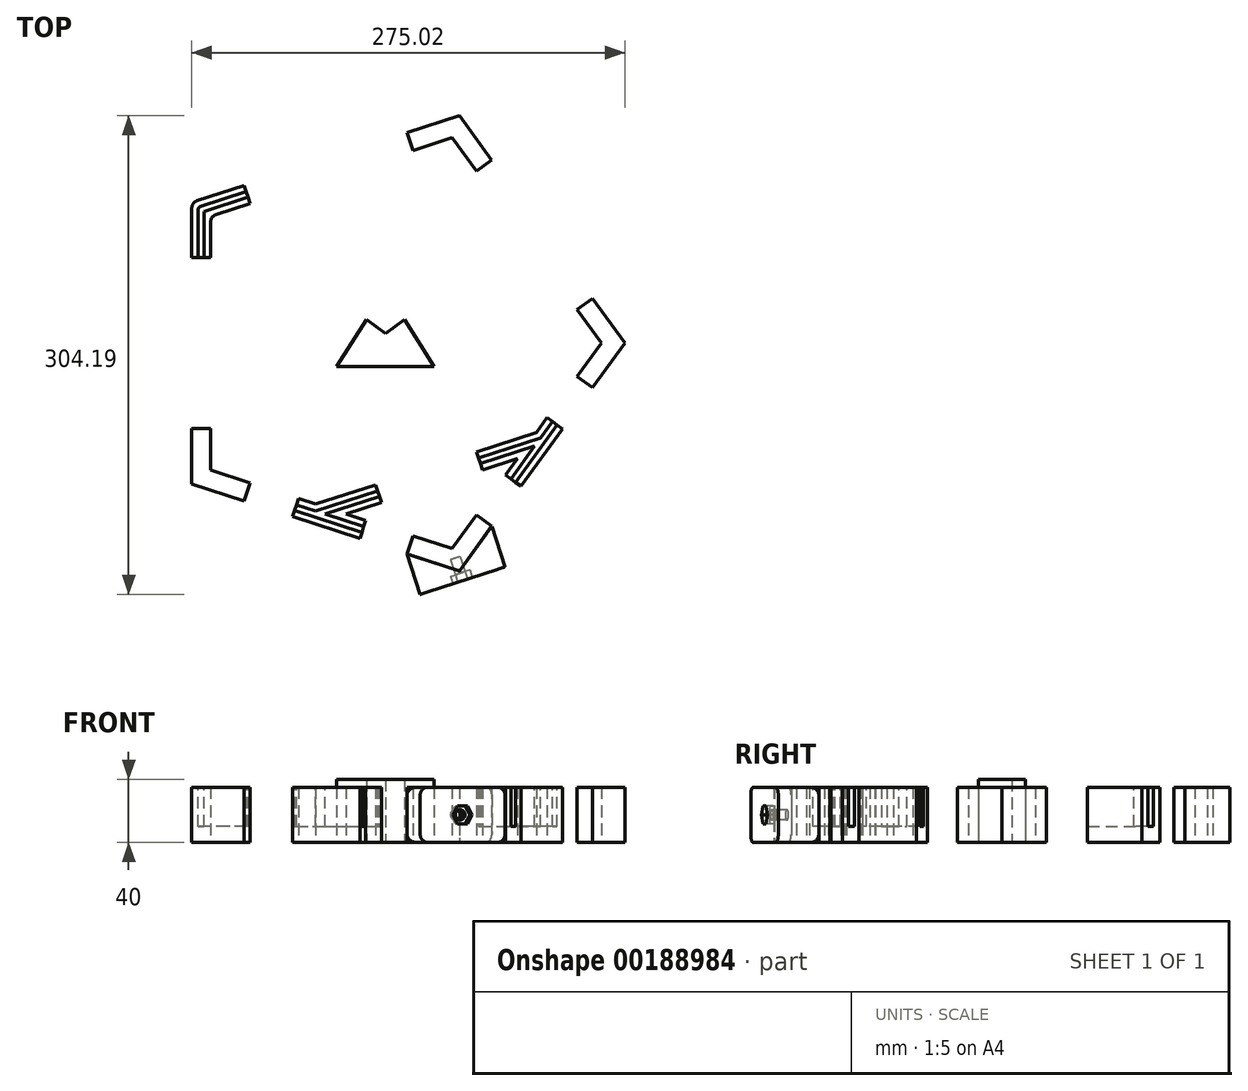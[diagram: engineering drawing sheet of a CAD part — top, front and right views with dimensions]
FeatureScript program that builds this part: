
annotation { "Feature Type Name" : "Feature", "Feature Type Description" : "" }
export const myFeature = defineFeature(function(context is Context, id is Id, definition is map)
    precondition{}
    {
        {
            var Q0;
            Q0=qCreatedBy(makeId("Top.planeOp"),FACE);
            var sketch = newSketch(context, id + "F0", { "sketchPlane" : qUnion([Q0])});
            skCircle(sketch, "E0.cCircle", {"center": v(0, 0) * mm, "radius": 117 * mm, "construction": true});
            skLineSegment(sketch, "E0.0", {"start": v(-117, 85) * mm, "end": v(44.69, 137.53) * mm, "construction": true});
            skLineSegment(sketch, "E0.1", {"start": v(44.69, 137.53) * mm, "end": v(144.61, 0) * mm, "construction": true});
            skLineSegment(sketch, "E0.2", {"start": v(144.61, 0) * mm, "end": v(44.69, -137.53) * mm, "construction": true});
            skLineSegment(sketch, "E0.3", {"start": v(44.69, -137.53) * mm, "end": v(-117, -85) * mm, "construction": true});
            skLineSegment(sketch, "E0.4", {"start": v(-117, -85) * mm, "end": v(-117, 85) * mm, "construction": true});
            skPoint(sketch, "E0.0.midPoint", {"position": v(-36.15, 111.27) * mm});
            skLineSegment(sketch, "E1", {"start": v(-123, 89.36) * mm, "end": v(-89.7, 100.17) * mm});
            skLineSegment(sketch, "E2", {"start": v(-123, 54.36) * mm, "end": v(-123, 89.36) * mm});
            skLineSegment(sketch, "E3.MirrorCS", {"start": v(-111, 54.36) * mm, "end": v(-111, 80.64) * mm});
            skLineSegment(sketch, "E4.MirrorCS", {"start": v(-111, 80.64) * mm, "end": v(-86, 88.76) * mm});
            skPoint(sketch, "E5.orphan", {"position": v(-127.63, 87.85) * mm});
            skPoint(sketch, "E6.orphan", {"position": v(-123, 104.04) * mm});
            skPoint(sketch, "E7.orphan", {"position": v(-111, 104.04) * mm});
            skPoint(sketch, "E8.orphan", {"position": v(-123.92, 76.44) * mm});
            skLineSegment(sketch, "E9", {"start": v(-123, 54.36) * mm, "end": v(-111, 54.36) * mm});
            skLineSegment(sketch, "E10", {"start": v(-86, 88.76) * mm, "end": v(-89.7, 100.17) * mm});
            skPoint(sketch, "E11.MirrorP", {"position": v(-127.63, -87.85) * mm});
            skPoint(sketch, "E12.MirrorP", {"position": v(-123, -104.04) * mm});
            skPoint(sketch, "E13.MirrorP", {"position": v(-111, -104.04) * mm});
            skPoint(sketch, "E14.MirrorP", {"position": v(-123.92, -76.44) * mm});
            skLineSegment(sketch, "E15.MirrorCS", {"start": v(-86, -88.76) * mm, "end": v(-89.7, -100.17) * mm});
            skLineSegment(sketch, "E16.MirrorCS", {"start": v(-123, -54.36) * mm, "end": v(-111, -54.36) * mm});
            skLineSegment(sketch, "E17.MirrorCS", {"start": v(-111, -80.64) * mm, "end": v(-86, -88.76) * mm});
            skLineSegment(sketch, "E18.MirrorCS", {"start": v(-111, -54.36) * mm, "end": v(-111, -80.64) * mm});
            skLineSegment(sketch, "E19.MirrorCS", {"start": v(-123, -54.36) * mm, "end": v(-123, -89.36) * mm});
            skLineSegment(sketch, "E20.MirrorCS", {"start": v(-123, -89.36) * mm, "end": v(-89.7, -100.17) * mm});
            skLineSegment(sketch, "E21.MirrorCS", {"start": v(-117, 85) * mm, "end": v(-117, -85) * mm, "construction": true});
            skLineSegment(sketch, "E22.MirrorCS", {"start": v(-117, -85) * mm, "end": v(44.69, -137.53) * mm, "construction": true});
            skLineSegment(sketch, "E23", {"start": v(-36.15, -111.27) * mm, "end": v(-46.52, -143.17) * mm, "construction": true});
            skLineSegment(sketch, "E24.MirrorCS", {"start": v(44.69, -137.53) * mm, "end": v(144.61, 0) * mm, "construction": true});
            skPoint(sketch, "E25.MirrorP", {"position": v(51.62, -146.1) * mm});
            skLineSegment(sketch, "E26.MirrorCS", {"start": v(67.55, -116.27) * mm, "end": v(46.98, -144.59) * mm});
            skPoint(sketch, "E27.MirrorP", {"position": v(160.66, 11.88) * mm});
            skLineSegment(sketch, "E28.MirrorCS", {"start": v(17.4, -122.36) * mm, "end": v(13.7, -133.77) * mm});
            skLineSegment(sketch, "E29.MirrorCS", {"start": v(121.75, 21.26) * mm, "end": v(131.45, 28.32) * mm});
            skLineSegment(sketch, "E30.MirrorCS", {"start": v(131.45, -28.32) * mm, "end": v(121.75, -21.26) * mm});
            skLineSegment(sketch, "E31.MirrorCS", {"start": v(137.2, 0) * mm, "end": v(121.75, 21.26) * mm});
            skLineSegment(sketch, "E32.MirrorCS", {"start": v(121.75, -21.26) * mm, "end": v(137.2, 0) * mm});
            skLineSegment(sketch, "E33.MirrorCS", {"start": v(131.45, -28.32) * mm, "end": v(152.03, 0) * mm});
            skLineSegment(sketch, "E34.MirrorCS", {"start": v(152.03, 0) * mm, "end": v(131.45, 28.32) * mm});
            skPoint(sketch, "E35.MirrorP", {"position": v(28.64, -149.41) * mm});
            skPoint(sketch, "E36.MirrorP", {"position": v(55.33, -134.68) * mm});
            skPoint(sketch, "E37.MirrorP", {"position": v(150.95, 18.93) * mm});
            skPoint(sketch, "E38.MirrorP", {"position": v(154.9, -3.95) * mm});
            skLineSegment(sketch, "E39.MirrorCS", {"start": v(67.55, -116.27) * mm, "end": v(57.84, -109.22) * mm});
            skLineSegment(sketch, "E40.MirrorCS", {"start": v(46.98, -144.59) * mm, "end": v(13.7, -133.77) * mm});
            skLineSegment(sketch, "E41.MirrorCS", {"start": v(42.4, -130.48) * mm, "end": v(17.4, -122.36) * mm});
            skLineSegment(sketch, "E42.MirrorCS", {"start": v(57.84, -109.22) * mm, "end": v(42.4, -130.48) * mm});
            skPoint(sketch, "E43.MirrorP", {"position": v(38.35, -156.47) * mm});
            skPoint(sketch, "E44.MirrorP", {"position": v(145.19, -11) * mm});
            skLineSegment(sketch, "E45", {"start": v(94.65, 68.77) * mm, "end": v(113.34, 82.34) * mm, "construction": true});
            skLineSegment(sketch, "E46.MirrorCS", {"start": v(44.69, 137.53) * mm, "end": v(-117, 85) * mm, "construction": true});
            skLineSegment(sketch, "E47.MirrorCS", {"start": v(46.98, 144.59) * mm, "end": v(67.55, 116.27) * mm});
            skPoint(sketch, "E48.MirrorP", {"position": v(60.94, 149.12) * mm});
            skPoint(sketch, "E49.MirrorP", {"position": v(44.11, 148.53) * mm});
            skPoint(sketch, "E50.MirrorP", {"position": v(34.4, 141.48) * mm});
            skLineSegment(sketch, "E51.MirrorCS", {"start": v(13.7, 133.77) * mm, "end": v(46.98, 144.59) * mm});
            skLineSegment(sketch, "E52.MirrorCS", {"start": v(42.4, 130.48) * mm, "end": v(57.84, 109.22) * mm});
            skPoint(sketch, "E53.MirrorP", {"position": v(64.65, 137.71) * mm});
            skLineSegment(sketch, "E54.MirrorCS", {"start": v(144.61, 0) * mm, "end": v(44.69, 137.53) * mm, "construction": true});
            skLineSegment(sketch, "E55.MirrorCS", {"start": v(57.84, 109.22) * mm, "end": v(67.55, 116.27) * mm});
            skLineSegment(sketch, "E56.MirrorCS", {"start": v(17.4, 122.36) * mm, "end": v(42.4, 130.48) * mm});
            skLineSegment(sketch, "E57.MirrorCS", {"start": v(13.7, 133.77) * mm, "end": v(17.4, 122.36) * mm});
            skLineSegment(sketch, "E58", {"start": v(-81.04, -120.55) * mm, "end": v(144.28, -47.34) * mm, "construction": true});
            skLineSegment(sketch, "E59", {"start": v(44.69, -137.53) * mm, "end": v(54.4, -134.38) * mm});
            skLineSegment(sketch, "E60", {"start": v(-16.2, -124.06) * mm, "end": v(-59, -110.15) * mm});
            skLineSegment(sketch, "E61.MirrorCS", {"start": v(-12.49, -112.65) * mm, "end": v(-24.89, -108.62) * mm});
            skLineSegment(sketch, "E62", {"start": v(-44.3, -102.3) * mm, "end": v(-6.26, -89.95) * mm});
            skLineSegment(sketch, "E63.MirrorCS", {"start": v(-34.6, -111.77) * mm, "end": v(-34.58, -111.77) * mm});
            skLineSegment(sketch, "E64", {"start": v(-55.29, -98.74) * mm, "end": v(-59, -110.15) * mm});
            skLineSegment(sketch, "E65", {"start": v(-12.49, -112.65) * mm, "end": v(-16.2, -124.06) * mm});
            skPoint(sketch, "E66.orphan", {"position": v(-40.6, -113.72) * mm});
            skLineSegment(sketch, "E67.trimOffspring", {"start": v(-24.89, -108.62) * mm, "end": v(-2.55, -101.36) * mm});
            skLineSegment(sketch, "E68.trimOffspring", {"start": v(-44.3, -102.3) * mm, "end": v(-55.29, -98.74) * mm});
            skLineSegment(sketch, "E69", {"start": v(-6.26, -89.95) * mm, "end": v(-2.55, -101.36) * mm});
            skLineSegment(sketch, "E70", {"start": v(-36.15, 111.27) * mm, "end": v(42.4, -130.48) * mm, "construction": true});
            skLineSegment(sketch, "E71.MirrorCS", {"start": v(93.69, -70.1) * mm, "end": v(93.67, -70.1) * mm});
            skLineSegment(sketch, "E72.MirrorCS", {"start": v(102.77, -47.39) * mm, "end": v(112.47, -54.44) * mm});
            skLineSegment(sketch, "E73.MirrorCS", {"start": v(95.98, -56.73) * mm, "end": v(102.77, -47.39) * mm});
            skLineSegment(sketch, "E74.MirrorCS", {"start": v(76.32, -83.8) * mm, "end": v(86.02, -90.85) * mm});
            skLineSegment(sketch, "E75.MirrorCS", {"start": v(95.98, -56.73) * mm, "end": v(57.94, -69.09) * mm});
            skPoint(sketch, "E76.MirrorP", {"position": v(99.69, -68.14) * mm});
            skLineSegment(sketch, "E77.MirrorCS", {"start": v(83.98, -73.24) * mm, "end": v(61.64, -80.5) * mm});
            skLineSegment(sketch, "E78.MirrorCS", {"start": v(86.02, -90.85) * mm, "end": v(112.47, -54.44) * mm});
            skLineSegment(sketch, "E79.MirrorCS", {"start": v(57.94, -69.09) * mm, "end": v(61.64, -80.5) * mm});
            skLineSegment(sketch, "E80.MirrorCS", {"start": v(76.32, -83.8) * mm, "end": v(83.98, -73.24) * mm});
            skLineSegment(sketch, "E81", {"start": v(22.07, -159.6) * mm, "end": v(75.94, -142.1) * mm});
            skLineSegment(sketch, "E82", {"start": v(67.59, -116.39) * mm, "end": v(75.94, -142.1) * mm});
            skLineSegment(sketch, "E83.MirrorCS", {"start": v(13.73, -133.89) * mm, "end": v(22.08, -159.6) * mm});
            skLineSegment(sketch, "E84", {"start": v(13.73, -133.89) * mm, "end": v(47.02, -144.7) * mm});
            skLineSegment(sketch, "E85", {"start": v(67.59, -116.39) * mm, "end": v(47.02, -144.7) * mm});
            skPoint(sketch, "E86.orphan", {"position": v(67.68, -116.27) * mm});
            skPoint(sketch, "E87.orphan", {"position": v(13.7, -133.77) * mm});
            skSolve(sketch);
        }
        {
            var Q0;
            Q0 = qSketchRegion(id + "F0", true);
            extrude(context, id + "F1", {"entities" : qUnion([Q0]), "depth" : 35 * mm});
        }
        {
            var Q0;
            Q0=makeQuery(id+"F1.opExtrude","CAP_FACE",FACE,{"disambiguationData":[OSD([sQuery(id+"F0.wireOp",EDGE,"E1"),sQuery(id+"F0.wireOp",EDGE,"E2"),sQuery(id+"F0.wireOp",EDGE,"E3.MirrorCS"),sQuery(id+"F0.wireOp",EDGE,"E4.MirrorCS"),sQuery(id+"F0.wireOp",EDGE,"E9"),sQuery(id+"F0.wireOp",EDGE,"E10")])],"isStart":false});
            var sketch = newSketch(context, id + "F2", { "sketchPlane" : qUnion([Q0])});
            skLineSegment(sketch, "E88", {"start": v(-117, 54.36) * mm, "end": v(-117, 85) * mm});
            skLineSegment(sketch, "E89", {"start": v(-87.85, 94.47) * mm, "end": v(-117, 85) * mm});
            skPoint(sketch, "E90.orphan", {"position": v(-117, 84.36) * mm});
            skPoint(sketch, "E91.orphan", {"position": v(-118.96, 84.36) * mm});
            skArc(sketch, "E92.0.startCap", {"start": v(-115.12, 54.36) * mm, "mid": v(-117, 52.48) * mm, "end": v(-118.87, 54.36) * mm});
            skArc(sketch, "E92.0.endCap", {"start": v(-118.87, 85) * mm, "mid": v(-117, 86.87) * mm, "end": v(-115.12, 85) * mm});
            skLineSegment(sketch, "E92.0.left", {"start": v(-118.87, 54.36) * mm, "end": v(-118.87, 85) * mm});
            skLineSegment(sketch, "E92.0.right", {"start": v(-115.12, 54.36) * mm, "end": v(-115.12, 85) * mm});
            skArc(sketch, "E92.1.startCap", {"start": v(-88.43, 96.25) * mm, "mid": v(-86.07, 95.05) * mm, "end": v(-87.27, 92.69) * mm});
            skArc(sketch, "E92.1.endCap", {"start": v(-116.41, 83.22) * mm, "mid": v(-118.78, 84.42) * mm, "end": v(-117.57, 86.78) * mm});
            skLineSegment(sketch, "E92.1.left", {"start": v(-87.27, 92.69) * mm, "end": v(-116.41, 83.22) * mm});
            skLineSegment(sketch, "E92.1.right", {"start": v(-88.43, 96.25) * mm, "end": v(-117.57, 86.78) * mm});
            skLineSegment(sketch, "E93", {"start": v(-44.3, -108.62) * mm, "end": v(99.69, -61.83) * mm});
            skLineSegment(sketch, "E94", {"start": v(113.08, -43.4) * mm, "end": v(77.1, -92.92) * mm});
            skLineSegment(sketch, "E95", {"start": v(-66.96, -101.26) * mm, "end": v(-1.1, -122.66) * mm});
            skPoint(sketch, "E96.end.orphan", {"position": v(64.77, -144.06) * mm});
            skArc(sketch, "E97.0.startCap", {"start": v(-43.73, -110.4) * mm, "mid": v(-46.09, -109.2) * mm, "end": v(-44.88, -106.83) * mm});
            skArc(sketch, "E97.0.endCap", {"start": v(99.1, -60.05) * mm, "mid": v(101.47, -61.25) * mm, "end": v(100.27, -63.62) * mm});
            skLineSegment(sketch, "E97.0.left", {"start": v(-44.88, -106.83) * mm, "end": v(99.1, -60.05) * mm});
            skLineSegment(sketch, "E97.0.right", {"start": v(-43.73, -110.4) * mm, "end": v(100.27, -63.62) * mm});
            skArc(sketch, "E97.1.startCap", {"start": v(-67.54, -103.04) * mm, "mid": v(-68.74, -100.68) * mm, "end": v(-66.38, -99.47) * mm});
            skArc(sketch, "E97.1.endCap", {"start": v(-0.51, -120.87) * mm, "mid": v(0.7, -123.24) * mm, "end": v(-1.67, -124.44) * mm});
            skLineSegment(sketch, "E97.1.left", {"start": v(-66.38, -99.47) * mm, "end": v(-0.51, -120.87) * mm});
            skLineSegment(sketch, "E97.1.right", {"start": v(-67.54, -103.04) * mm, "end": v(-1.67, -124.44) * mm});
            skArc(sketch, "E97.2.startCap", {"start": v(111.56, -42.3) * mm, "mid": v(114.18, -41.88) * mm, "end": v(114.6, -44.5) * mm});
            skArc(sketch, "E97.2.endCap", {"start": v(78.61, -94.03) * mm, "mid": v(76, -94.44) * mm, "end": v(75.58, -91.82) * mm});
            skLineSegment(sketch, "E97.2.left", {"start": v(114.6, -44.5) * mm, "end": v(78.61, -94.03) * mm});
            skLineSegment(sketch, "E97.2.right", {"start": v(111.56, -42.3) * mm, "end": v(75.58, -91.82) * mm});
            skSolve(sketch);
        }
        {
            var Q0;
            {var subQ0=sQuery(id+"F2.wireOp",EDGE,"E97.1.endCap");Q0=makeQuery(id+"F2.imprint","IMPRINT",FACE,{"disambiguationData":[TD([[makeQuery(id+"F2.imprint","IMPRINT",EDGE,{"derivedFrom":subQ0}),-1.0]])]});}
            var Q1;
            {var subQ5=sQuery(id+"F2.wireOp",EDGE,"E97.1.startCap");Q1=makeQuery(id+"F2.imprint","IMPRINT",FACE,{"disambiguationData":[TD([[makeQuery(id+"F2.imprint","IMPRINT",EDGE,{"derivedFrom":subQ5}),-1.0]])]});}
            var Q2;
            {var subQ8=sQuery(id+"F2.wireOp",EDGE,"E97.2.startCap");Q2=makeQuery(id+"F2.imprint","IMPRINT",FACE,{"disambiguationData":[TD([[makeQuery(id+"F2.imprint","IMPRINT",EDGE,{"derivedFrom":subQ8}),-1.0]])]});}
            var Q3;
            {var subQ5=sQuery(id+"F2.wireOp",EDGE,"E97.2.endCap");Q3=makeQuery(id+"F2.imprint","IMPRINT",FACE,{"disambiguationData":[TD([[makeQuery(id+"F2.imprint","IMPRINT",EDGE,{"derivedFrom":subQ5}),-1.0]])]});}
            var Q4;
            {var subQ3=sQuery(id+"F2.wireOp",EDGE,"E89");var subQ7=sQuery(id+"F2.wireOp",EDGE,"E88");var subQ8=makeQuery(id+"F2.imprint","INTERSECT",VERTEX,{"derivedFrom":[subQ7,subQ3]});Q4=makeQuery(id+"F2.imprint","IMPRINT",FACE,{"disambiguationData":[TD([[makeQuery(id+"F2.imprint","IMPRINT",EDGE,{"disambiguationData":[TD([[subQ8,1.0]])],"derivedFrom":subQ7}),-1.0]])]});}
            var Q5;
            {var subQ0=sQuery(id+"F2.wireOp",EDGE,"E97.1.left");var subQ1=sQuery(id+"F2.wireOp",EDGE,"E93");var subQ2=makeQuery(id+"F2.imprint","INTERSECT",VERTEX,{"derivedFrom":[subQ1,subQ0]});Q5=makeQuery(id+"F2.imprint","IMPRINT",FACE,{"disambiguationData":[TD([[makeQuery(id+"F2.imprint","IMPRINT",EDGE,{"disambiguationData":[TD([[subQ2,-1.0]])],"derivedFrom":subQ1}),1.0]])]});}
            var Q6;
            {var subQ2=sQuery(id+"F2.wireOp",EDGE,"E88");var subQ6=sQuery(id+"F2.wireOp",EDGE,"E89");var subQ8=makeQuery(id+"F2.imprint","INTERSECT",VERTEX,{"derivedFrom":[subQ2,subQ6]});Q6=makeQuery(id+"F2.imprint","IMPRINT",FACE,{"disambiguationData":[TD([[makeQuery(id+"F2.imprint","IMPRINT",EDGE,{"disambiguationData":[TD([[subQ8,1.0]])],"derivedFrom":subQ2}),1.0]])]});}
            var Q7;
            {var subQ3=sQuery(id+"F2.wireOp",EDGE,"E95");var subQ7=sQuery(id+"F2.wireOp",EDGE,"E93");var subQ8=makeQuery(id+"F2.imprint","INTERSECT",VERTEX,{"derivedFrom":[subQ7,subQ3]});Q7=makeQuery(id+"F2.imprint","IMPRINT",FACE,{"disambiguationData":[TD([[makeQuery(id+"F2.imprint","IMPRINT",EDGE,{"disambiguationData":[TD([[subQ8,-1.0]])],"derivedFrom":subQ7}),1.0]])]});}
            var Q8;
            {var subQ0=sQuery(id+"F2.wireOp",EDGE,"E95");var subQ1=sQuery(id+"F2.wireOp",EDGE,"E93");var subQ2=makeQuery(id+"F2.imprint","INTERSECT",VERTEX,{"derivedFrom":[subQ1,subQ0]});Q8=makeQuery(id+"F2.imprint","IMPRINT",FACE,{"disambiguationData":[TD([[makeQuery(id+"F2.imprint","IMPRINT",EDGE,{"disambiguationData":[TD([[subQ2,-1.0]])],"derivedFrom":subQ1}),-1.0]])]});}
            var Q9;
            {var subQ5=sQuery(id+"F2.wireOp",EDGE,"E94");var subQ6=sQuery(id+"F2.wireOp",EDGE,"E93");var subQ7=makeQuery(id+"F2.imprint","INTERSECT",VERTEX,{"derivedFrom":[subQ6,subQ5]});Q9=makeQuery(id+"F2.imprint","IMPRINT",FACE,{"disambiguationData":[TD([[makeQuery(id+"F2.imprint","IMPRINT",EDGE,{"disambiguationData":[TD([[subQ7,1.0]])],"derivedFrom":subQ6}),1.0]])]});}
            var Q10;
            {var subQ0=sQuery(id+"F2.wireOp",EDGE,"E94");var subQ1=sQuery(id+"F2.wireOp",EDGE,"E93");var subQ2=makeQuery(id+"F2.imprint","INTERSECT",VERTEX,{"derivedFrom":[subQ1,subQ0]});Q10=makeQuery(id+"F2.imprint","IMPRINT",FACE,{"disambiguationData":[TD([[makeQuery(id+"F2.imprint","IMPRINT",EDGE,{"disambiguationData":[TD([[subQ2,1.0]])],"derivedFrom":subQ1}),-1.0]])]});}
            var Q11;
            {var subQ4=sQuery(id+"F2.wireOp",EDGE,"E94");var subQ5=makeQuery(id+"F2.imprint","INTERSECT",VERTEX,{"derivedFrom":[sQuery(id+"F2.wireOp",EDGE,"E93"),subQ4]});Q11=makeQuery(id+"F2.imprint","IMPRINT",FACE,{"disambiguationData":[TD([[makeQuery(id+"F2.imprint","IMPRINT",EDGE,{"disambiguationData":[TD([[subQ5,1.0]])],"derivedFrom":subQ4}),1.0]])]});}
            var Q12;
            {var subQ1=sQuery(id+"F2.wireOp",EDGE,"E95");var subQ4=makeQuery(id+"F2.imprint","INTERSECT",VERTEX,{"derivedFrom":[sQuery(id+"F2.wireOp",EDGE,"E93"),subQ1]});Q12=makeQuery(id+"F2.imprint","IMPRINT",FACE,{"disambiguationData":[TD([[makeQuery(id+"F2.imprint","IMPRINT",EDGE,{"disambiguationData":[TD([[subQ4,1.0]])],"derivedFrom":subQ1}),-1.0]])]});}
            var Q13;
            {var subQ5=sQuery(id+"F2.wireOp",EDGE,"E92.0.left");Q13=makeQuery(id+"F2.imprint","IMPRINT",FACE,{"disambiguationData":[TD([[makeQuery(id+"F2.imprint","IMPRINT",EDGE,{"derivedFrom":subQ5}),-1.0]])]});}
            var Q14;
            {var subQ5=sQuery(id+"F2.wireOp",EDGE,"E88");var subQ7=makeQuery(id+"F1.opExtrude","CAP_EDGE",EDGE,{"disambiguationData":[OSD([sQuery(id+"F0.wireOp",EDGE,"E9")])],"isStart":false});var subQ9=makeQuery(id+"F2.imprint","INTERSECT",VERTEX,{"derivedFrom":[subQ7,subQ5]});Q14=makeQuery(id+"F2.imprint","IMPRINT",FACE,{"disambiguationData":[TD([[makeQuery(id+"F2.imprint","IMPRINT",EDGE,{"disambiguationData":[TD([[subQ9,-1.0]])],"derivedFrom":subQ5}),-1.0]])]});}
            var Q15;
            {var subQ5=sQuery(id+"F2.wireOp",EDGE,"E92.1.right");Q15=makeQuery(id+"F2.imprint","IMPRINT",FACE,{"disambiguationData":[TD([[makeQuery(id+"F2.imprint","IMPRINT",EDGE,{"derivedFrom":subQ5}),1.0]])]});}
            var Q16;
            {var subQ1=makeQuery(id+"F1.opExtrude","CAP_EDGE",EDGE,{"disambiguationData":[OSD([sQuery(id+"F0.wireOp",EDGE,"E10")])],"isStart":false});var subQ7=sQuery(id+"F2.wireOp",EDGE,"E89");var subQ9=makeQuery(id+"F2.imprint","INTERSECT",VERTEX,{"derivedFrom":[subQ1,subQ7]});Q16=makeQuery(id+"F2.imprint","IMPRINT",FACE,{"disambiguationData":[TD([[makeQuery(id+"F2.imprint","IMPRINT",EDGE,{"disambiguationData":[TD([[subQ9,-1.0]])],"derivedFrom":subQ7}),1.0]])]});}
            var Q17;
            {var subQ0=sQuery(id+"F2.wireOp",EDGE,"E92.0.startCap");Q17=makeQuery(id+"F2.imprint","IMPRINT",FACE,{"disambiguationData":[TD([[makeQuery(id+"F2.imprint","IMPRINT",EDGE,{"derivedFrom":subQ0}),-1.0]])]});}
            var Q18;
            {var subQ0=sQuery(id+"F2.wireOp",EDGE,"E92.1.startCap");Q18=makeQuery(id+"F2.imprint","IMPRINT",FACE,{"disambiguationData":[TD([[makeQuery(id+"F2.imprint","IMPRINT",EDGE,{"derivedFrom":subQ0}),-1.0]])]});}
            extrude(context, id + "F3", {"entities" : qUnion([Q0, Q1, Q2, Q3, Q4, Q5, Q6, Q7, Q8, Q9, Q10, Q11, Q12, Q13, Q14, Q15, Q16, Q17, Q18]), "operationType" : NewBodyOperationType.REMOVE, "oppositeDirection" : true, "depth" : 25 * mm});
        }
        {
            var Q0;
            Q0=makeQuery(id+"F1.opExtrude","SWEPT_EDGE",EDGE,{"disambiguationData":[OSD([sQuery(id+"F0.wireOp",EDGE,"E3.MirrorCS"),sQuery(id+"F0.wireOp",EDGE,"E4.MirrorCS")])]});
            var Q1;
            Q1=makeQuery(id+"F1.opExtrude","SWEPT_EDGE",EDGE,{"disambiguationData":[OSD([sQuery(id+"F0.wireOp",EDGE,"E1"),sQuery(id+"F0.wireOp",EDGE,"E2")])]});
            fillet(context, id + "F4", {"entities" : qUnion([Q0, Q1]), "radius" : 5 * mm, "tangentPropagation" : true, "allowEdgeOverflow" : false});
        }
        {
            var Q0;
            Q0=makeQuery(id+"F1.opExtrude","CAP_FACE",FACE,{"disambiguationData":[OSD([sQuery(id+"F0.wireOp",EDGE,"E60"),sQuery(id+"F0.wireOp",EDGE,"E61.MirrorCS"),sQuery(id+"F0.wireOp",EDGE,"E62"),sQuery(id+"F0.wireOp",EDGE,"E64"),sQuery(id+"F0.wireOp",EDGE,"E65"),sQuery(id+"F0.wireOp",EDGE,"E67.trimOffspring"),sQuery(id+"F0.wireOp",EDGE,"E68.trimOffspring"),sQuery(id+"F0.wireOp",EDGE,"E69")])],"isStart":false});
            var sketch = newSketch(context, id + "F5", { "sketchPlane" : qUnion([Q0])});
            skLineSegment(sketch, "E98", {"start": v(-44.3, -108.62) * mm, "end": v(99.69, -61.83) * mm});
            skLineSegment(sketch, "E99", {"start": v(112.9, -43.64) * mm, "end": v(76.92, -93.16) * mm});
            skLineSegment(sketch, "E100", {"start": v(-67.46, -101.1) * mm, "end": v(-1.6, -122.5) * mm});
            skPoint(sketch, "E101.end.orphan", {"position": v(64.27, -143.9) * mm});
            skArc(sketch, "E102.0.startCap", {"start": v(-43.73, -110.4) * mm, "mid": v(-46.09, -109.2) * mm, "end": v(-44.88, -106.83) * mm});
            skArc(sketch, "E102.0.endCap", {"start": v(99.1, -60.05) * mm, "mid": v(101.47, -61.25) * mm, "end": v(100.27, -63.62) * mm});
            skLineSegment(sketch, "E102.0.left", {"start": v(-44.88, -106.83) * mm, "end": v(99.1, -60.05) * mm});
            skLineSegment(sketch, "E102.0.right", {"start": v(-43.73, -110.4) * mm, "end": v(100.27, -63.62) * mm});
            skArc(sketch, "E102.1.startCap", {"start": v(-68.04, -102.88) * mm, "mid": v(-69.25, -100.51) * mm, "end": v(-66.88, -99.3) * mm});
            skArc(sketch, "E102.1.endCap", {"start": v(-1.02, -120.71) * mm, "mid": v(0.19, -123.07) * mm, "end": v(-2.18, -124.28) * mm});
            skLineSegment(sketch, "E102.1.left", {"start": v(-66.88, -99.3) * mm, "end": v(-1.02, -120.71) * mm});
            skLineSegment(sketch, "E102.1.right", {"start": v(-68.04, -102.88) * mm, "end": v(-2.18, -124.28) * mm});
            skArc(sketch, "E102.2.startCap", {"start": v(111.4, -42.53) * mm, "mid": v(114, -42.12) * mm, "end": v(114.42, -44.74) * mm});
            skArc(sketch, "E102.2.endCap", {"start": v(78.44, -94.27) * mm, "mid": v(75.82, -94.68) * mm, "end": v(75.4, -92.06) * mm});
            skLineSegment(sketch, "E102.2.left", {"start": v(114.42, -44.74) * mm, "end": v(78.44, -94.27) * mm});
            skLineSegment(sketch, "E102.2.right", {"start": v(111.4, -42.53) * mm, "end": v(75.4, -92.06) * mm});
            skSolve(sketch);
        }
        {
            var Q0;
            {var subQ1=sQuery(id+"F5.wireOp",EDGE,"E102.1.startCap");Q0=makeQuery(id+"F5.imprint","IMPRINT",FACE,{"disambiguationData":[TD([[makeQuery(id+"F5.imprint","IMPRINT",EDGE,{"derivedFrom":subQ1}),-1.0]])]});}
            var Q1;
            {var subQ5=sQuery(id+"F5.wireOp",EDGE,"E102.0.startCap");var subQ7=sQuery(id+"F5.wireOp",EDGE,"E100");var subQ8=makeQuery(id+"F5.imprint","INTERSECT",VERTEX,{"derivedFrom":[subQ7,subQ5]});Q1=makeQuery(id+"F5.imprint","IMPRINT",FACE,{"disambiguationData":[TD([[makeQuery(id+"F5.imprint","IMPRINT",EDGE,{"disambiguationData":[TD([[subQ8,1.0]])],"derivedFrom":subQ7}),1.0]])]});}
            var Q2;
            {var subQ0=sQuery(id+"F5.wireOp",EDGE,"E102.0.startCap");var subQ1=sQuery(id+"F5.wireOp",EDGE,"E100");var subQ2=makeQuery(id+"F5.imprint","INTERSECT",VERTEX,{"derivedFrom":[subQ1,subQ0]});Q2=makeQuery(id+"F5.imprint","IMPRINT",FACE,{"disambiguationData":[TD([[makeQuery(id+"F5.imprint","IMPRINT",EDGE,{"disambiguationData":[TD([[subQ2,1.0]])],"derivedFrom":subQ1}),-1.0]])]});}
            var Q3;
            {var subQ1=sQuery(id+"F5.wireOp",EDGE,"E100");var subQ6=makeQuery(id+"F5.imprint","INTERSECT",VERTEX,{"derivedFrom":[sQuery(id+"F5.wireOp",EDGE,"E98"),subQ1]});Q3=makeQuery(id+"F5.imprint","IMPRINT",FACE,{"disambiguationData":[TD([[makeQuery(id+"F5.imprint","IMPRINT",EDGE,{"disambiguationData":[TD([[subQ6,1.0]])],"derivedFrom":subQ1}),-1.0]])]});}
            var Q4;
            {var subQ3=sQuery(id+"F5.wireOp",EDGE,"E100");var subQ5=sQuery(id+"F5.wireOp",EDGE,"E98");var subQ6=makeQuery(id+"F5.imprint","INTERSECT",VERTEX,{"derivedFrom":[subQ5,subQ3]});Q4=makeQuery(id+"F5.imprint","IMPRINT",FACE,{"disambiguationData":[TD([[makeQuery(id+"F5.imprint","IMPRINT",EDGE,{"disambiguationData":[TD([[subQ6,-1.0]])],"derivedFrom":subQ5}),1.0]])]});}
            var Q5;
            {var subQ0=sQuery(id+"F5.wireOp",EDGE,"E100");var subQ1=sQuery(id+"F5.wireOp",EDGE,"E98");var subQ2=makeQuery(id+"F5.imprint","INTERSECT",VERTEX,{"derivedFrom":[subQ1,subQ0]});Q5=makeQuery(id+"F5.imprint","IMPRINT",FACE,{"disambiguationData":[TD([[makeQuery(id+"F5.imprint","IMPRINT",EDGE,{"disambiguationData":[TD([[subQ2,-1.0]])],"derivedFrom":subQ1}),-1.0]])]});}
            var Q6;
            {var subQ0=sQuery(id+"F5.wireOp",EDGE,"E102.1.left");var subQ1=sQuery(id+"F5.wireOp",EDGE,"E98");var subQ2=makeQuery(id+"F5.imprint","INTERSECT",VERTEX,{"derivedFrom":[subQ1,subQ0]});Q6=makeQuery(id+"F5.imprint","IMPRINT",FACE,{"disambiguationData":[TD([[makeQuery(id+"F5.imprint","IMPRINT",EDGE,{"disambiguationData":[TD([[subQ2,-1.0]])],"derivedFrom":subQ1}),1.0]])]});}
            var Q7;
            {var subQ0=sQuery(id+"F5.wireOp",EDGE,"E102.1.left");var subQ1=sQuery(id+"F5.wireOp",EDGE,"E98");var subQ2=makeQuery(id+"F5.imprint","INTERSECT",VERTEX,{"derivedFrom":[subQ1,subQ0]});Q7=makeQuery(id+"F5.imprint","IMPRINT",FACE,{"disambiguationData":[TD([[makeQuery(id+"F5.imprint","IMPRINT",EDGE,{"disambiguationData":[TD([[subQ2,-1.0]])],"derivedFrom":subQ1}),-1.0]])]});}
            var Q8;
            {var subQ0=sQuery(id+"F5.wireOp",EDGE,"E102.0.right");var subQ1=sQuery(id+"F5.wireOp",EDGE,"E100");var subQ2=makeQuery(id+"F5.imprint","INTERSECT",VERTEX,{"derivedFrom":[subQ1,subQ0]});Q8=makeQuery(id+"F5.imprint","IMPRINT",FACE,{"disambiguationData":[TD([[makeQuery(id+"F5.imprint","IMPRINT",EDGE,{"disambiguationData":[TD([[subQ2,-1.0]])],"derivedFrom":subQ1}),1.0]])]});}
            var Q9;
            {var subQ5=sQuery(id+"F5.wireOp",EDGE,"E102.0.right");var subQ7=sQuery(id+"F5.wireOp",EDGE,"E100");var subQ8=makeQuery(id+"F5.imprint","INTERSECT",VERTEX,{"derivedFrom":[subQ7,subQ5]});Q9=makeQuery(id+"F5.imprint","IMPRINT",FACE,{"disambiguationData":[TD([[makeQuery(id+"F5.imprint","IMPRINT",EDGE,{"disambiguationData":[TD([[subQ8,-1.0]])],"derivedFrom":subQ7}),-1.0]])]});}
            var Q10;
            {var subQ1=sQuery(id+"F5.wireOp",EDGE,"E102.1.endCap");Q10=makeQuery(id+"F5.imprint","IMPRINT",FACE,{"disambiguationData":[TD([[makeQuery(id+"F5.imprint","IMPRINT",EDGE,{"derivedFrom":subQ1}),-1.0]])]});}
            var Q11;
            {var subQ0=sQuery(id+"F5.wireOp",EDGE,"E102.2.right");var subQ1=sQuery(id+"F5.wireOp",EDGE,"E98");var subQ2=makeQuery(id+"F5.imprint","INTERSECT",VERTEX,{"derivedFrom":[subQ1,subQ0]});Q11=makeQuery(id+"F5.imprint","IMPRINT",FACE,{"disambiguationData":[TD([[makeQuery(id+"F5.imprint","IMPRINT",EDGE,{"disambiguationData":[TD([[subQ2,1.0]])],"derivedFrom":subQ1}),-1.0]])]});}
            var Q12;
            {var subQ0=sQuery(id+"F5.wireOp",EDGE,"E102.2.right");var subQ1=sQuery(id+"F5.wireOp",EDGE,"E98");var subQ2=makeQuery(id+"F5.imprint","INTERSECT",VERTEX,{"derivedFrom":[subQ1,subQ0]});Q12=makeQuery(id+"F5.imprint","IMPRINT",FACE,{"disambiguationData":[TD([[makeQuery(id+"F5.imprint","IMPRINT",EDGE,{"disambiguationData":[TD([[subQ2,1.0]])],"derivedFrom":subQ1}),1.0]])]});}
            var Q13;
            {var subQ4=sQuery(id+"F5.wireOp",EDGE,"E99");var subQ6=makeQuery(id+"F5.imprint","INTERSECT",VERTEX,{"derivedFrom":[sQuery(id+"F5.wireOp",EDGE,"E98"),subQ4]});Q13=makeQuery(id+"F5.imprint","IMPRINT",FACE,{"disambiguationData":[TD([[makeQuery(id+"F5.imprint","IMPRINT",EDGE,{"disambiguationData":[TD([[subQ6,1.0]])],"derivedFrom":subQ4}),1.0]])]});}
            var Q14;
            {var subQ5=sQuery(id+"F5.wireOp",EDGE,"E99");var subQ6=sQuery(id+"F5.wireOp",EDGE,"E98");var subQ7=makeQuery(id+"F5.imprint","INTERSECT",VERTEX,{"derivedFrom":[subQ6,subQ5]});Q14=makeQuery(id+"F5.imprint","IMPRINT",FACE,{"disambiguationData":[TD([[makeQuery(id+"F5.imprint","IMPRINT",EDGE,{"disambiguationData":[TD([[subQ7,1.0]])],"derivedFrom":subQ6}),1.0]])]});}
            var Q15;
            {var subQ0=sQuery(id+"F5.wireOp",EDGE,"E99");var subQ1=sQuery(id+"F5.wireOp",EDGE,"E98");var subQ2=makeQuery(id+"F5.imprint","INTERSECT",VERTEX,{"derivedFrom":[subQ1,subQ0]});Q15=makeQuery(id+"F5.imprint","IMPRINT",FACE,{"disambiguationData":[TD([[makeQuery(id+"F5.imprint","IMPRINT",EDGE,{"disambiguationData":[TD([[subQ2,1.0]])],"derivedFrom":subQ1}),-1.0]])]});}
            var Q16;
            {var subQ0=sQuery(id+"F5.wireOp",EDGE,"E102.2.endCap");Q16=makeQuery(id+"F5.imprint","IMPRINT",FACE,{"disambiguationData":[TD([[makeQuery(id+"F5.imprint","IMPRINT",EDGE,{"derivedFrom":subQ0}),-1.0]])]});}
            var Q17;
            {var subQ0=sQuery(id+"F5.wireOp",EDGE,"E102.2.startCap");Q17=makeQuery(id+"F5.imprint","IMPRINT",FACE,{"disambiguationData":[TD([[makeQuery(id+"F5.imprint","IMPRINT",EDGE,{"derivedFrom":subQ0}),-1.0]])]});}
            extrude(context, id + "F6", {"entities" : qUnion([Q0, Q1, Q2, Q3, Q4, Q5, Q6, Q7, Q8, Q9, Q10, Q11, Q12, Q13, Q14, Q15, Q16, Q17]), "operationType" : NewBodyOperationType.REMOVE, "oppositeDirection" : true, "depth" : 25 * mm});
        }
        {
            var Q0;
            Q0=makeQuery(id+"F1.opExtrude","CAP_FACE",FACE,{"disambiguationData":[OSD([sQuery(id+"F0.wireOp",EDGE,"E72.MirrorCS"),sQuery(id+"F0.wireOp",EDGE,"E73.MirrorCS"),sQuery(id+"F0.wireOp",EDGE,"E74.MirrorCS"),sQuery(id+"F0.wireOp",EDGE,"E75.MirrorCS"),sQuery(id+"F0.wireOp",EDGE,"E77.MirrorCS"),sQuery(id+"F0.wireOp",EDGE,"E78.MirrorCS"),sQuery(id+"F0.wireOp",EDGE,"E79.MirrorCS"),sQuery(id+"F0.wireOp",EDGE,"E80.MirrorCS")])],"isStart":false});
            var sketch = newSketch(context, id + "F7", { "sketchPlane" : qUnion([Q0])});
            skLineSegment(sketch, "E103", {"start": v(-44.5, -108.68) * mm, "end": v(99.69, -61.83) * mm});
            skLineSegment(sketch, "E104", {"start": v(113.1, -43.36) * mm, "end": v(77.12, -92.9) * mm});
            skLineSegment(sketch, "E105", {"start": v(-66.52, -101.53) * mm, "end": v(-0.65, -122.93) * mm});
            skPoint(sketch, "E106.end.orphan", {"position": v(65.22, -144.33) * mm});
            skArc(sketch, "E107.0.startCap", {"start": v(-43.92, -110.47) * mm, "mid": v(-46.29, -109.26) * mm, "end": v(-45.08, -106.9) * mm});
            skArc(sketch, "E107.0.endCap", {"start": v(99.1, -60.05) * mm, "mid": v(101.47, -61.25) * mm, "end": v(100.27, -63.62) * mm});
            skLineSegment(sketch, "E107.0.left", {"start": v(-45.08, -106.9) * mm, "end": v(99.1, -60.05) * mm});
            skLineSegment(sketch, "E107.0.right", {"start": v(-43.92, -110.47) * mm, "end": v(100.27, -63.62) * mm});
            skArc(sketch, "E107.1.startCap", {"start": v(-67.1, -103.31) * mm, "mid": v(-68.3, -100.95) * mm, "end": v(-65.94, -99.75) * mm});
            skArc(sketch, "E107.1.endCap", {"start": v(-0.07, -121.15) * mm, "mid": v(1.13, -123.5) * mm, "end": v(-1.23, -124.71) * mm});
            skLineSegment(sketch, "E107.1.left", {"start": v(-65.94, -99.75) * mm, "end": v(-0.07, -121.15) * mm});
            skLineSegment(sketch, "E107.1.right", {"start": v(-67.1, -103.31) * mm, "end": v(-1.23, -124.71) * mm});
            skArc(sketch, "E107.2.startCap", {"start": v(111.59, -42.26) * mm, "mid": v(114.2, -41.85) * mm, "end": v(114.62, -44.47) * mm});
            skArc(sketch, "E107.2.endCap", {"start": v(78.64, -94) * mm, "mid": v(76.02, -94.4) * mm, "end": v(75.6, -91.79) * mm});
            skLineSegment(sketch, "E107.2.left", {"start": v(114.62, -44.47) * mm, "end": v(78.64, -94) * mm});
            skLineSegment(sketch, "E107.2.right", {"start": v(111.59, -42.26) * mm, "end": v(75.6, -91.79) * mm});
            skSolve(sketch);
        }
        {
            var Q0;
            {var subQ4=sQuery(id+"F7.wireOp",EDGE,"E107.2.endCap");Q0=makeQuery(id+"F7.imprint","IMPRINT",FACE,{"disambiguationData":[TD([[makeQuery(id+"F7.imprint","IMPRINT",EDGE,{"derivedFrom":subQ4}),-1.0]])]});}
            var Q1;
            {var subQ5=sQuery(id+"F7.wireOp",EDGE,"E107.0.right");var subQ7=sQuery(id+"F7.wireOp",EDGE,"E104");var subQ8=makeQuery(id+"F7.imprint","INTERSECT",VERTEX,{"derivedFrom":[subQ7,subQ5]});Q1=makeQuery(id+"F7.imprint","IMPRINT",FACE,{"disambiguationData":[TD([[makeQuery(id+"F7.imprint","IMPRINT",EDGE,{"disambiguationData":[TD([[subQ8,-1.0]])],"derivedFrom":subQ7}),1.0]])]});}
            var Q2;
            {var subQ0=sQuery(id+"F7.wireOp",EDGE,"E107.0.right");var subQ1=sQuery(id+"F7.wireOp",EDGE,"E104");var subQ2=makeQuery(id+"F7.imprint","INTERSECT",VERTEX,{"derivedFrom":[subQ1,subQ0]});Q2=makeQuery(id+"F7.imprint","IMPRINT",FACE,{"disambiguationData":[TD([[makeQuery(id+"F7.imprint","IMPRINT",EDGE,{"disambiguationData":[TD([[subQ2,-1.0]])],"derivedFrom":subQ1}),-1.0]])]});}
            var Q3;
            {var subQ0=sQuery(id+"F7.wireOp",EDGE,"E104");var subQ1=sQuery(id+"F7.wireOp",EDGE,"E103");var subQ2=makeQuery(id+"F7.imprint","INTERSECT",VERTEX,{"derivedFrom":[subQ1,subQ0]});Q3=makeQuery(id+"F7.imprint","IMPRINT",FACE,{"disambiguationData":[TD([[makeQuery(id+"F7.imprint","IMPRINT",EDGE,{"disambiguationData":[TD([[subQ2,1.0]])],"derivedFrom":subQ1}),-1.0]])]});}
            var Q4;
            {var subQ0=sQuery(id+"F7.wireOp",EDGE,"E107.2.right");var subQ1=sQuery(id+"F7.wireOp",EDGE,"E103");var subQ2=makeQuery(id+"F7.imprint","INTERSECT",VERTEX,{"derivedFrom":[subQ1,subQ0]});Q4=makeQuery(id+"F7.imprint","IMPRINT",FACE,{"disambiguationData":[TD([[makeQuery(id+"F7.imprint","IMPRINT",EDGE,{"disambiguationData":[TD([[subQ2,1.0]])],"derivedFrom":subQ1}),1.0]])]});}
            var Q5;
            {var subQ5=sQuery(id+"F7.wireOp",EDGE,"E104");var subQ7=sQuery(id+"F7.wireOp",EDGE,"E103");var subQ8=makeQuery(id+"F7.imprint","INTERSECT",VERTEX,{"derivedFrom":[subQ7,subQ5]});Q5=makeQuery(id+"F7.imprint","IMPRINT",FACE,{"disambiguationData":[TD([[makeQuery(id+"F7.imprint","IMPRINT",EDGE,{"disambiguationData":[TD([[subQ8,1.0]])],"derivedFrom":subQ7}),1.0]])]});}
            var Q6;
            {var subQ5=sQuery(id+"F7.wireOp",EDGE,"E107.0.endCap");var subQ7=sQuery(id+"F7.wireOp",EDGE,"E104");var subQ8=makeQuery(id+"F7.imprint","INTERSECT",VERTEX,{"derivedFrom":[subQ7,subQ5]});Q6=makeQuery(id+"F7.imprint","IMPRINT",FACE,{"disambiguationData":[TD([[makeQuery(id+"F7.imprint","IMPRINT",EDGE,{"disambiguationData":[TD([[subQ8,1.0]])],"derivedFrom":subQ7}),-1.0]])]});}
            var Q7;
            {var subQ0=sQuery(id+"F7.wireOp",EDGE,"E107.0.endCap");var subQ1=sQuery(id+"F7.wireOp",EDGE,"E104");var subQ2=makeQuery(id+"F7.imprint","INTERSECT",VERTEX,{"derivedFrom":[subQ1,subQ0]});Q7=makeQuery(id+"F7.imprint","IMPRINT",FACE,{"disambiguationData":[TD([[makeQuery(id+"F7.imprint","IMPRINT",EDGE,{"disambiguationData":[TD([[subQ2,1.0]])],"derivedFrom":subQ1}),1.0]])]});}
            var Q8;
            {var subQ4=sQuery(id+"F7.wireOp",EDGE,"E107.2.startCap");Q8=makeQuery(id+"F7.imprint","IMPRINT",FACE,{"disambiguationData":[TD([[makeQuery(id+"F7.imprint","IMPRINT",EDGE,{"derivedFrom":subQ4}),-1.0]])]});}
            var Q9;
            {var subQ4=sQuery(id+"F7.wireOp",EDGE,"E104");var subQ6=makeQuery(id+"F7.imprint","INTERSECT",VERTEX,{"derivedFrom":[sQuery(id+"F7.wireOp",EDGE,"E103"),subQ4]});Q9=makeQuery(id+"F7.imprint","IMPRINT",FACE,{"disambiguationData":[TD([[makeQuery(id+"F7.imprint","IMPRINT",EDGE,{"disambiguationData":[TD([[subQ6,1.0]])],"derivedFrom":subQ4}),1.0]])]});}
            var Q10;
            {var subQ0=sQuery(id+"F7.wireOp",EDGE,"E107.2.right");var subQ1=sQuery(id+"F7.wireOp",EDGE,"E103");var subQ2=makeQuery(id+"F7.imprint","INTERSECT",VERTEX,{"derivedFrom":[subQ1,subQ0]});Q10=makeQuery(id+"F7.imprint","IMPRINT",FACE,{"disambiguationData":[TD([[makeQuery(id+"F7.imprint","IMPRINT",EDGE,{"disambiguationData":[TD([[subQ2,1.0]])],"derivedFrom":subQ1}),-1.0]])]});}
            extrude(context, id + "F8", {"entities" : qUnion([Q0, Q1, Q2, Q3, Q4, Q5, Q6, Q7, Q8, Q9, Q10]), "operationType" : NewBodyOperationType.REMOVE, "oppositeDirection" : true, "depth" : 25 * mm});
        }
        {
            var Q0;
            Q0=makeQuery(id+"F1.opExtrude","CAP_EDGE",EDGE,{"disambiguationData":[OSD([sQuery(id+"F0.wireOp",EDGE,"E83.MirrorCS")])],"isStart":true});
            var Q1;
            Q1=makeQuery(id+"F1.opExtrude","CAP_EDGE",EDGE,{"disambiguationData":[OSD([sQuery(id+"F0.wireOp",EDGE,"E83.MirrorCS")])],"isStart":false});
            var Q2;
            Q2=makeQuery(id+"F1.opExtrude","CAP_EDGE",EDGE,{"disambiguationData":[OSD([sQuery(id+"F0.wireOp",EDGE,"E82")])],"isStart":false});
            var Q3;
            Q3=makeQuery(id+"F1.opExtrude","CAP_EDGE",EDGE,{"disambiguationData":[OSD([sQuery(id+"F0.wireOp",EDGE,"E82")])],"isStart":true});
            fillet(context, id + "F9", {"entities" : qUnion([Q0, Q1, Q2, Q3]), "radius" : 5 * mm, "tangentPropagation" : true, "allowEdgeOverflow" : false});
        }
        {
            var Q0;
            Q0=makeQuery(id+"F1.opExtrude","SWEPT_FACE",FACE,{"disambiguationData":[OSD([sQuery(id+"F0.wireOp",EDGE,"E81")])]});
            var sketch = newSketch(context, id + "F10", { "sketchPlane" : qUnion([Q0])});
            skLineSegment(sketch, "E108", {"start": v(-28.32, 17.5) * mm, "end": v(28.32, 17.5) * mm, "construction": true});
            skLineSegment(sketch, "E109", {"start": v(0, 35) * mm, "end": v(0, 0) * mm, "construction": true});
            skCircle(sketch, "E110.cCircle", {"center": v(0, 17.5) * mm, "radius": 5.6 * mm, "construction": true});
            skLineSegment(sketch, "E110.0", {"start": v(-3.23, 23.1) * mm, "end": v(3.23, 23.1) * mm});
            skLineSegment(sketch, "E110.1", {"start": v(3.23, 23.1) * mm, "end": v(6.47, 17.5) * mm});
            skLineSegment(sketch, "E110.2", {"start": v(6.47, 17.5) * mm, "end": v(3.23, 11.9) * mm});
            skLineSegment(sketch, "E110.3", {"start": v(3.23, 11.9) * mm, "end": v(-3.23, 11.9) * mm});
            skLineSegment(sketch, "E110.4", {"start": v(-3.23, 11.9) * mm, "end": v(-6.47, 17.5) * mm});
            skLineSegment(sketch, "E110.5", {"start": v(-6.47, 17.5) * mm, "end": v(-3.23, 23.1) * mm});
            skPoint(sketch, "E110.0.midPoint", {"position": v(0, 23.1) * mm});
            skSolve(sketch);
        }
        {
            var Q0;
            Q0=makeQuery(id+"F10.imprint","IMPRINT",FACE,{"disambiguationData":[TD([[makeQuery(id+"F10.imprint","IMPRINT",EDGE,{"derivedFrom":sQuery(id+"F10.wireOp",EDGE,"E110.0")}),1.0]])]});
            var sketch = newSketch(context, id + "F11", { "sketchPlane" : qUnion([Q0])});
            skCircle(sketch, "E111", {"center": v(0, 17.5) * mm, "radius": 3.25 * mm});
            skSolve(sketch);
        }
        {
            var Q0;
            Q0 = qSketchRegion(id + "F10", true);
            extrude(context, id + "F12", {"entities" : qUnion([Q0]), "operationType" : NewBodyOperationType.REMOVE, "oppositeDirection" : true, "depth" : 5 * mm});
        }
        {
            var Q0;
            Q0=makeQuery(id+"F11.imprint","IMPRINT",FACE,{"disambiguationData":[TD([[makeQuery(id+"F11.imprint","IMPRINT",EDGE,{"derivedFrom":sQuery(id+"F11.wireOp",EDGE,"E111")}),1.0]])]});
            var Q1;
            Q1=sQuery(id+"F11.wireOp",EDGE,"E111");
            extrude(context, id + "F13", {"entities" : qUnion([Q0]), "operationType" : NewBodyOperationType.REMOVE, "surfaceEntities" : qUnion([Q1]), "oppositeDirection" : true, "depth" : 15 * mm});
        }
        {
            var Q0;
            Q0=qCreatedBy(makeId("Top.planeOp"),FACE);
            var sketch = newSketch(context, id + "F14", { "sketchPlane" : qUnion([Q0])});
            skLineSegment(sketch, "E112.top", {"start": v(31, -15) * mm, "end": v(-31, -15) * mm});
            skPoint(sketch, "E112.middle", {"position": v(0, 0) * mm});
            skPoint(sketch, "E113", {"position": v(0, 6.18) * mm});
            skLineSegment(sketch, "E114", {"start": v(-31, -15) * mm, "end": v(-12.14, 15) * mm});
            skLineSegment(sketch, "E115", {"start": v(-12.14, 15) * mm, "end": v(0, 6.18) * mm});
            skPoint(sketch, "E112.right.start.orphan", {"position": v(-31, 15) * mm});
            skLineSegment(sketch, "E116.MirrorCS", {"start": v(12.14, 15) * mm, "end": v(0, 6.18) * mm});
            skLineSegment(sketch, "E117.MirrorCS", {"start": v(31, -15) * mm, "end": v(12.14, 15) * mm});
            skPoint(sketch, "E112.left.start.orphan", {"position": v(31, 15) * mm});
            skSolve(sketch);
        }
        {
            var Q0;
            Q0 = qSketchRegion(id + "F14", true);
            extrude(context, id + "F15", {"entities" : qUnion([Q0]), "depth" : 40 * mm});
        }
    });
